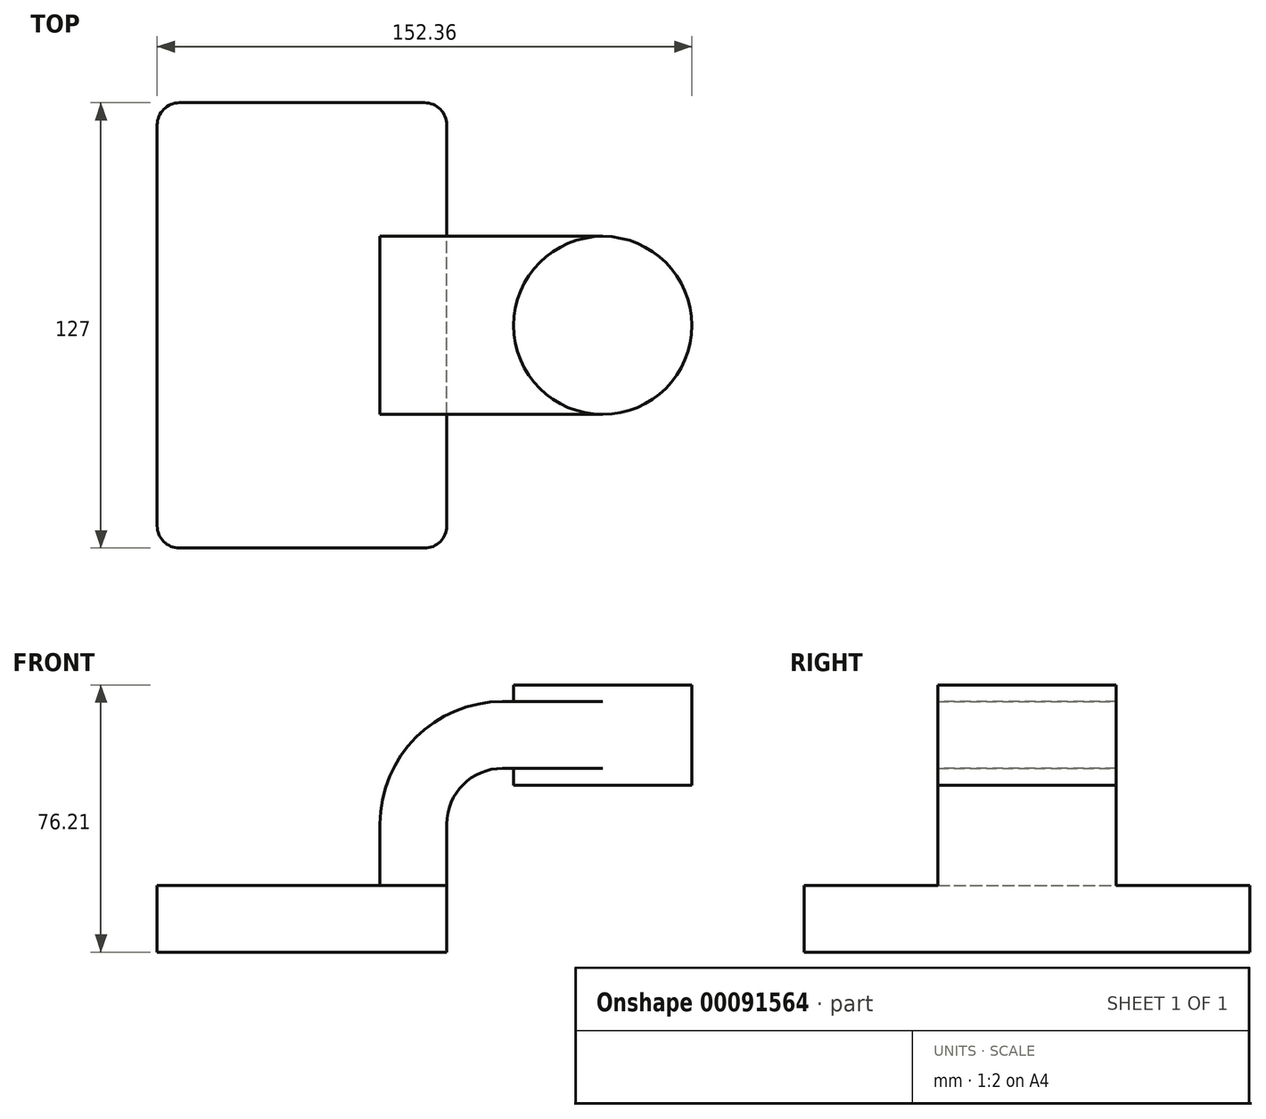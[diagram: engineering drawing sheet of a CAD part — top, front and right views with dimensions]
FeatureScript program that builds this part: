
annotation { "Feature Type Name" : "Feature", "Feature Type Description" : "" }
export const myFeature = defineFeature(function(context is Context, id is Id, definition is map)
    precondition{}
    {
        {
            var Q0;
            Q0=qCreatedBy(makeId("Front.planeOp"),FACE);
            var sketch = newSketch(context, id + "F0", { "sketchPlane" : qUnion([Q0])});
            skLineSegment(sketch, "E0.bottom", {"start": v(-41.28, 9.52) * mm, "end": v(41.28, 9.53) * mm});
            skLineSegment(sketch, "E0.top", {"start": v(-41.28, -9.53) * mm, "end": v(41.28, -9.53) * mm});
            skLineSegment(sketch, "E0.left", {"start": v(-41.28, 9.52) * mm, "end": v(-41.27, -9.53) * mm});
            skLineSegment(sketch, "E0.right", {"start": v(41.28, 9.53) * mm, "end": v(41.28, -9.52) * mm});
            skPoint(sketch, "E0.middle", {"position": v(0, 0) * mm});
            skLineSegment(sketch, "E1", {"start": v(41.28, 9.53) * mm, "end": v(41.28, 27) * mm});
            skArc(sketch, "E2", {"start": v(41.28, 27) * mm, "mid": v(45.92, 38.23) * mm, "end": v(57.15, 42.88) * mm});
            skLineSegment(sketch, "E3", {"start": v(57.15, 42.88) * mm, "end": v(85.73, 42.88) * mm});
            skLineSegment(sketch, "E4.0", {"start": v(57.15, 61.93) * mm, "end": v(85.7, 61.93) * mm});
            skArc(sketch, "E4.1", {"start": v(22.23, 27) * mm, "mid": v(32.45, 51.7) * mm, "end": v(57.15, 61.93) * mm});
            skLineSegment(sketch, "E4.2", {"start": v(22.23, 9.53) * mm, "end": v(22.23, 27) * mm});
            skLineSegment(sketch, "E5.bottom", {"start": v(60.3, 66.67) * mm, "end": v(111.1, 66.67) * mm});
            skLineSegment(sketch, "E5.top", {"start": v(60.3, 38.1) * mm, "end": v(111.1, 38.1) * mm});
            skLineSegment(sketch, "E5.left", {"start": v(60.3, 66.67) * mm, "end": v(60.3, 38.1) * mm});
            skLineSegment(sketch, "E5.right", {"start": v(111.1, 66.68) * mm, "end": v(111.1, 38.1) * mm});
            skPoint(sketch, "E5.middle", {"position": v(85.7, 52.39) * mm});
            skFitSpline(sketch, "E6", {"points": [v(-41.28, 9.52) * mm, v(57.15, 61.93) * mm], "startDerivative": vector(1.43, 148.88) * mm, "endDerivative": vector(171.45, -0.44) * mm});
            skLineSegment(sketch, "E7", {"start": v(85.7, 66.67) * mm, "end": v(85.7, 38.1) * mm});
            skSolve(sketch);
        }
        {
            var Q0;
            Q0=makeQuery(id+"F0.imprint","IMPRINT",FACE,{"disambiguationData":[TD([[makeQuery(id+"F0.imprint","IMPRINT",EDGE,{"derivedFrom":sQuery(id+"F0.wireOp",EDGE,"E0.top")}),1.0]])]});
            extrude(context, id + "F1", {"entities" : qUnion([Q0]), "endBound" : BoundingType.SYMMETRIC, "depth" : 127 * mm});
        }
        {
            var Q0;
            {var subQ6=sQuery(id+"F0.wireOp",EDGE,"E1");Q0=makeQuery(id+"F0.imprint","IMPRINT",FACE,{"disambiguationData":[TD([[makeQuery(id+"F0.imprint","IMPRINT",EDGE,{"derivedFrom":subQ6}),1.0]])]});}
            var Q1;
            {var subQ0=sQuery(id+"F0.wireOp",EDGE,"E5.left");var subQ1=sQuery(id+"F0.wireOp",EDGE,"E3");var subQ2=makeQuery(id+"F0.imprint","INTERSECT",VERTEX,{"derivedFrom":[subQ1,subQ0]});Q1=makeQuery(id+"F0.imprint","IMPRINT",FACE,{"disambiguationData":[TD([[makeQuery(id+"F0.imprint","IMPRINT",EDGE,{"disambiguationData":[TD([[subQ2,-1.0]])],"derivedFrom":subQ1}),1.0]])]});}
            extrude(context, id + "F2", {"entities" : qUnion([Q0, Q1]), "operationType" : NewBodyOperationType.ADD, "endBound" : BoundingType.SYMMETRIC, "depth" : 50.8 * mm});
        }
        {
            var Q0;
            Q0=makeQuery(id+"F0.imprint","IMPRINT",FACE,{"disambiguationData":[TD([[makeQuery(id+"F0.imprint","IMPRINT",EDGE,{"derivedFrom":sQuery(id+"F0.wireOp",EDGE,"E4.1")}),1.0]])]});
            extrude(context, id + "F3", {"entities" : qUnion([Q0]), "operationType" : NewBodyOperationType.ADD, "endBound" : BoundingType.SYMMETRIC, "depth" : 15.88 * mm});
        }
        {
            var Q0;
            {var subQ5=sQuery(id+"F0.wireOp",EDGE,"E5.right");Q0=makeQuery(id+"F0.imprint","IMPRINT",FACE,{"disambiguationData":[TD([[makeQuery(id+"F0.imprint","IMPRINT",EDGE,{"derivedFrom":subQ5}),-1.0]])]});}
            var Q1;
            Q1=sQuery(id+"F0.wireOp",EDGE,"E7");
            revolve(context, id + "F4", {"operationType" : NewBodyOperationType.ADD, "entities" : qUnion([Q0]), "axis" : qUnion([Q1]), "revolveType" : RevolveType.FULL});
        }
        {
            var Q0;
            Q0=makeQuery(id+"F1.opExtrude","CAP_EDGE",EDGE,{"disambiguationData":[OSD([sQuery(id+"F0.wireOp",EDGE,"E0.right")])],"isStart":false});
            var Q1;
            Q1=makeQuery(id+"F1.opExtrude","CAP_EDGE",EDGE,{"disambiguationData":[OSD([sQuery(id+"F0.wireOp",EDGE,"E0.left")])],"isStart":false});
            var Q2;
            Q2=makeQuery(id+"F1.opExtrude","CAP_EDGE",EDGE,{"disambiguationData":[OSD([sQuery(id+"F0.wireOp",EDGE,"E0.right")])],"isStart":true});
            var Q3;
            Q3=makeQuery(id+"F1.opExtrude","CAP_EDGE",EDGE,{"disambiguationData":[OSD([sQuery(id+"F0.wireOp",EDGE,"E0.left")])],"isStart":true});
            fillet(context, id + "F5", {"entities" : qUnion([Q0, Q1, Q2, Q3]), "radius" : 6.35 * mm, "tangentPropagation" : true, "allowEdgeOverflow" : false});
        }
    });
